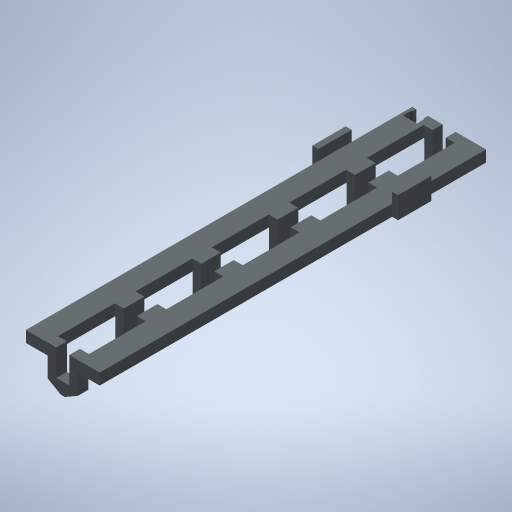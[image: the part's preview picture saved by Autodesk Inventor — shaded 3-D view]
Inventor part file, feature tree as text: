
AUTODESK INVENTOR PART (.ipt)
format: ipt  version: 2023 (Build 270158000, 158)  size: 347,648 bytes
history: native  units: mm
features: extrude x9, sketch x9, other x7
ambient origin geometry x8: Origin, YZ Plane, XZ Plane, XY Plane, X Axis, Y Axis, Z Axis, Center Point
bodies: Solid1 (feature_tree)
feature tree (25):
  extrude  "Extrusion1"  Depth=178.0mm TaperAngle=0.0deg
  extrude  "Extrusion2"  Depth=25.0mm TaperAngle=0.0deg
  extrude  "Extrusion3"  Depth=25.0mm TaperAngle=0.0deg
  extrude  "Extrusion4"  Depth=2.75mm TaperAngle=0.0deg
  extrude  "Extrusion5"  TaperAngle=0.0deg  [1 undecoded]
  extrude  "Extrusion6"  [1 undecoded]
  extrude  "Extrusion8"  [1 undecoded]
  extrude  "Extrusion9"  [1 undecoded]
  extrude  "Extrusion10"  [1 undecoded]
  other  "p1_XY"
  other  "p1_YZ"
  other  "p1_ZX"
  other  "p1_X"
  other  "p1_Y"
  other  "p1_Z"
  other  "p1_Center"
  sketch  "Sketch_1"  dims[d0=178.0mm d1=0.0mm d2=25.0mm d3=0.0mm]
  sketch  "Sketch_9"
  sketch  "Sketch_2"  dims[d4=25.0mm d5=0.0mm d6=25.0mm d7=0.0mm]
  sketch  "Sketch_3"  dims[d8=25.0mm d9=0.0mm d10=25.0mm d11=0.0mm]
  sketch  "Sketch_4"  dims[d14=6.0mm d15=0.0mm d16=2.75mm d17=0.0mm]
  sketch  "Sketch_5"  dims[d18=2.75mm d19=0.0mm d20=0.0mm]
  sketch  "Sketch_12"
  sketch  "Sketch_16"
  sketch  "Sketch_14"
note: 5 required parameter values undecoded (feature->parameter linkage not recoverable at this tier; creation-order binding heuristic only, values carry confidence <= 0.55)
